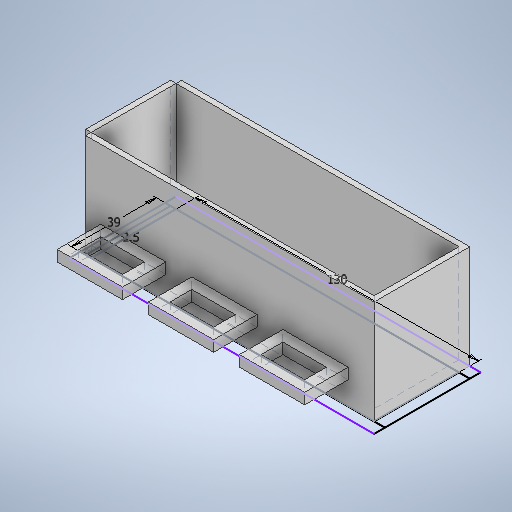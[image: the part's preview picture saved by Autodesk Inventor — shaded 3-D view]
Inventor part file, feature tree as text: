
AUTODESK INVENTOR PART (.ipt)
format: ipt  version: 2025 (Build 290162010, 162A)  size: 360,448 bytes
history: native  units: in
note: dims shown in document units (in); Inventor stores cm internally (conversion verified against a paired STEP export)
features: move_body x8, sketch x7, direct_edit x6, extrude x5
ambient origin geometry x8: Origin, YZ Plane, XZ Plane, XY Plane, X Axis, Y Axis, Z Axis, Center Point
bodies: Solid1 (feature_tree)
feature tree (26):
  sketch  "Sketch1"  dims[d0=5.1181in d1=1.5354in]
  extrude  "Extrusion1"  Depth=1.5354in
  sketch  "Sketch2"  dims[d2=0.1969in d3=0.0in d4=1.7717in d5=0.0in]
  sketch  "Sketch3"  dims[d6=0.0in d7=0.0in d8=-0.0984in d9=0.0in d10=0.0in d11=-0.0984in]
  sketch  "Sketch4"  dims[d12=0.0in d13=0.0in d14=-0.0984in d15=0.0in d16=0.0in d17=-0.0984in]
  sketch  "Sketch5"  dims[d18=1.1811in d19=0.1969in]
  extrude  "Extrusion2"  Depth=1.7717in TaperAngle=0.0deg
  direct_edit  "Direct Edit1"
  direct_edit  "Direct Edit2"
  sketch  "Sketch6"  dims[d20=0.4183in]
  direct_edit  "Direct Edit3"
  direct_edit  "Direct Edit4"
  extrude  "Extrusion3"  TaperAngle=0.0deg  [1 undecoded]
  direct_edit  "Direct Edit5"
  extrude  "Extrusion4"  TaperAngle=0.0deg  [1 undecoded]
  extrude  "Extrusion5"  Depth=0.1969in
  direct_edit  "Direct Edit6"
  sketch  "Sketch7"  dims[d21=0.0in d22=0.0in d23=-0.1969in d24=0.0in d25=0.0in d26=0.1969in d27=1.6732in d28=1.1811in d29=0.1969in d30=1.1811in d31=0.1969in d32=0.4675in d33=0.4675in d34=0.4675in d35=5.4134in d36=0.4675in d37=1.1811in d38=0.0in d39=0.0in d40=0.0in d41=-0.3937in d42=0.1969in d43=0.7874in d44=0.3937in d45=1.1811in d46=0.7874in d47=0.1969in d48=1.6486in d49=0.7874in d50=0.3937in d51=0.7874in d52=0.3937in d53=1.1811in d54=0.0in d55=0.0984in d56=1.1811in d57=0.0in d58=0.0in d59=0.0in d60=-0.0984in]
  move_body  "Move1"
  move_body  "Move2"
  move_body  "Move3"
  move_body  "Move4"
  move_body  "Move5"
  move_body  "Move6"
  move_body  "Move7"
  move_body  "Move8"
note: 2 required parameter values undecoded (feature->parameter linkage not recoverable at this tier; creation-order binding heuristic only, values carry confidence <= 0.55)
